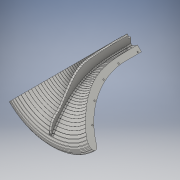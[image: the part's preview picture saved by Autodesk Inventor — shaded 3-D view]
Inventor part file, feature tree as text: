
AUTODESK INVENTOR PART (.ipt)
format: ipt  version: 2016 SP1 (Build 200210100, 210)  size: 3,730,432 bytes
history: native  units: in
note: dims shown in document units (in); Inventor stores cm internally (conversion verified against a paired STEP export)
features: hole x1, sketch x1, other x1
ambient origin geometry x8: Origin, YZ Plane, XZ Plane, XY Plane, X Axis, Y Axis, Z Axis, Center Point
bodies: Solid1 (feature_tree)
feature tree (3):
  hole  "Hole1"  [1 undecoded]
  sketch  "Sketch3"  dims[d0=0.516in d1=0.171in d2=0.432in d3=0.375in d4=0.25in d5=0.5635in d6=0.64in d7=0.8108in]
  parser-record x1  (decoder bookkeeping rows leaked as tree rows — omitted from the tree; the rows remain in map.json)
note: 1 required parameter value undecoded (feature->parameter linkage not recoverable at this tier; creation-order binding heuristic only, values carry confidence <= 0.55)
